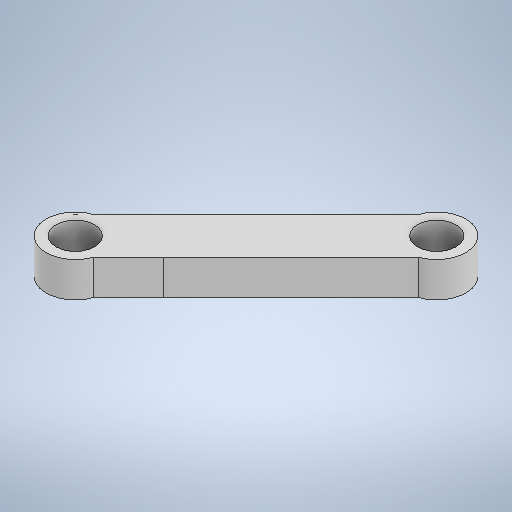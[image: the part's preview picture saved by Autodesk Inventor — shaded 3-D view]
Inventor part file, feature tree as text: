
AUTODESK INVENTOR PART (.ipt)
format: ipt  version: 2025.1 (Build 291241000, 241)  size: 274,944 bytes
history: native  units: in
note: dims shown in document units (in); Inventor stores cm internally (conversion verified against a paired STEP export)
features: extrude x1, sketch x1
ambient origin geometry x8: Origin, YZ Plane, XZ Plane, XY Plane, X Axis, Y Axis, Z Axis, Center Point
bodies: Solid1 (feature_tree)
feature tree (2):
  extrude  "Extrusion1"  Depth=0.1181in TaperAngle=0.0deg
  sketch  "Sketch1"  dims[d0=0.1969in d1=0.1969in d2=0.1181in d3=0.0in d4=0.1299in d5=0.1299in]
